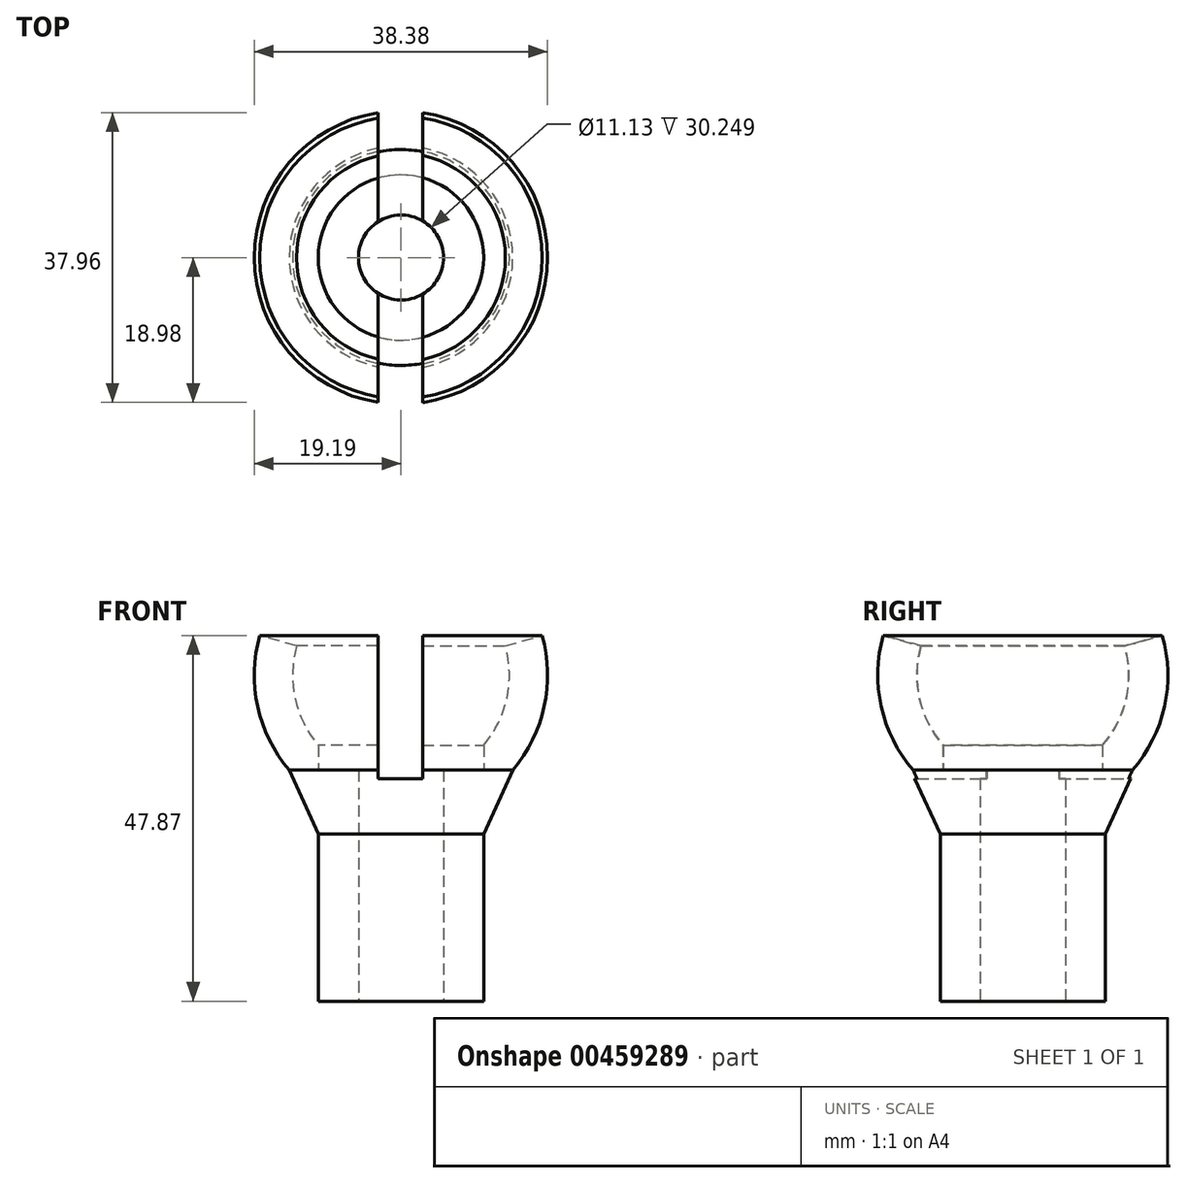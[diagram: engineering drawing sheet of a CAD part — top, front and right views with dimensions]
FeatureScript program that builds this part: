
annotation { "Feature Type Name" : "Feature", "Feature Type Description" : "" }
export const myFeature = defineFeature(function(context is Context, id is Id, definition is map)
    precondition{}
    {
        {
            var Q0;
            Q0=qCreatedBy(makeId("Front.planeOp"),FACE);
            var sketch = newSketch(context, id + "F0", { "sketchPlane" : qUnion([Q0])});
            skArc(sketch, "E0", {"start": v(-18.48, 22.74) * mm, "mid": v(-18.75, 13.45) * mm, "end": v(-14.63, 5.12) * mm});
            skArc(sketch, "E1.0", {"start": v(-13.66, 21.39) * mm, "mid": v(-13.87, 14.51) * mm, "end": v(-10.82, 8.35) * mm});
            skLineSegment(sketch, "E2", {"start": v(-18.48, 22.74) * mm, "end": v(-13.66, 21.39) * mm});
            skLineSegment(sketch, "E3", {"start": v(0, 1.5) * mm, "end": v(0, 32.49) * mm});
            skLineSegment(sketch, "E4", {"start": v(-10.82, 8.35) * mm, "end": v(-10.82, 5.12) * mm});
            skLineSegment(sketch, "E5", {"start": v(-10.82, -3.23) * mm, "end": v(-10.82, -25.13) * mm});
            skLineSegment(sketch, "E6", {"start": v(-10.82, -25.13) * mm, "end": v(-5.57, -25.13) * mm});
            skLineSegment(sketch, "E7", {"start": v(-5.57, -25.13) * mm, "end": v(-5.57, 5.12) * mm});
            skLineSegment(sketch, "E8", {"start": v(-5.57, 5.12) * mm, "end": v(-10.82, 5.12) * mm});
            skLineSegment(sketch, "E9", {"start": v(-14.63, 5.12) * mm, "end": v(-10.82, -3.23) * mm});
            skSolve(sketch);
        }
        {
            var Q0;
            Q0 = qSketchRegion(id + "F0", true);
            var Q1;
            Q1=sQuery(id+"F0.wireOp",EDGE,"E3");
            revolve(context, id + "F1", {"entities" : qUnion([Q0]), "axis" : qUnion([Q1]), "revolveType" : RevolveType.FULL});
        }
        {
            var Q0;
            Q0=qCreatedBy(makeId("Front.planeOp"),FACE);
            var sketch = newSketch(context, id + "F2", { "sketchPlane" : qUnion([Q0])});
            skLineSegment(sketch, "E10", {"start": v(0, 4.02) * mm, "end": v(-3.02, 4.02) * mm});
            skLineSegment(sketch, "E11", {"start": v(-3.02, 4.02) * mm, "end": v(-3.02, 26.08) * mm});
            skLineSegment(sketch, "E12", {"start": v(-3.02, 26.08) * mm, "end": v(2.83, 26.08) * mm});
            skLineSegment(sketch, "E13", {"start": v(2.83, 26.08) * mm, "end": v(2.83, 4.02) * mm});
            skLineSegment(sketch, "E14", {"start": v(2.83, 4.02) * mm, "end": v(0, 4.02) * mm});
            skSolve(sketch);
        }
        {
            var Q0;
            Q0 = qSketchRegion(id + "F2", true);
            extrude(context, id + "F3", {"entities" : qUnion([Q0]), "operationType" : NewBodyOperationType.REMOVE, "endBound" : BoundingType.THROUGH_ALL, "depth" : 25 * mm, "hasSecondDirection" : true, "secondDirectionOppositeDirection" : true, "secondDirectionDepth" : 25 * mm});
        }
    });
